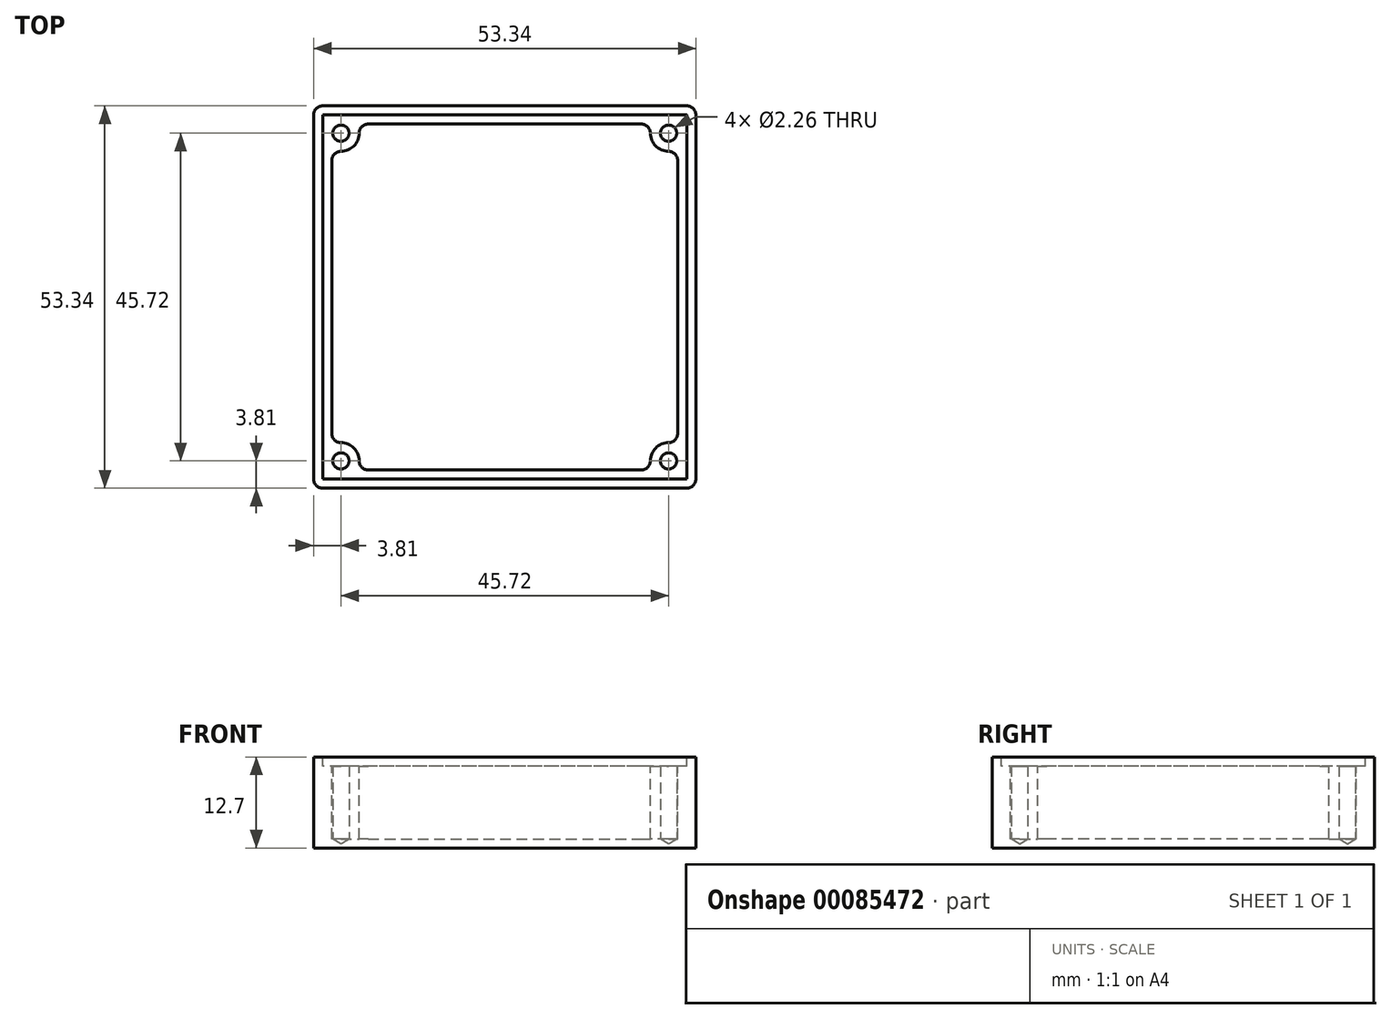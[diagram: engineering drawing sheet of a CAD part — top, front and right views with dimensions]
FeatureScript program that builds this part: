
annotation { "Feature Type Name" : "Feature", "Feature Type Description" : "" }
export const myFeature = defineFeature(function(context is Context, id is Id, definition is map)
    precondition{}
    {
        {
            var Q0;
            Q0=qCreatedBy(makeId("Top.planeOp"),FACE);
            var sketch = newSketch(context, id + "F0", { "sketchPlane" : qUnion([Q0])});
            skLineSegment(sketch, "E0.bottom", {"start": v(25.4, 25.4) * mm, "end": v(-25.4, 25.4) * mm, "construction": true});
            skLineSegment(sketch, "E0.top", {"start": v(25.4, -25.4) * mm, "end": v(-25.4, -25.4) * mm, "construction": true});
            skLineSegment(sketch, "E0.left", {"start": v(25.4, 25.4) * mm, "end": v(25.4, -25.4) * mm, "construction": true});
            skLineSegment(sketch, "E0.right", {"start": v(-25.4, 25.4) * mm, "end": v(-25.4, -25.4) * mm, "construction": true});
            skPoint(sketch, "E0.middle", {"position": v(0, 0) * mm});
            skLineSegment(sketch, "E1.bottom", {"start": v(26.67, 26.67) * mm, "end": v(-26.67, 26.67) * mm});
            skLineSegment(sketch, "E1.top", {"start": v(26.67, -26.67) * mm, "end": v(-26.67, -26.67) * mm});
            skLineSegment(sketch, "E1.left", {"start": v(26.67, 26.67) * mm, "end": v(26.67, -26.67) * mm});
            skLineSegment(sketch, "E1.right", {"start": v(-26.67, 26.67) * mm, "end": v(-26.67, -26.67) * mm});
            skSolve(sketch);
        }
        {
            var Q0;
            Q0 = qSketchRegion(id + "F0", true);
            extrude(context, id + "F1", {"entities" : qUnion([Q0]), "depth" : 12.7 * mm});
        }
        {
            var Q0;
            Q0=makeQuery(id+"F1.opExtrude","CAP_FACE",FACE,{"disambiguationData":[OSD([sQuery(id+"F0.wireOp",EDGE,"E1.bottom"),sQuery(id+"F0.wireOp",EDGE,"E1.top"),sQuery(id+"F0.wireOp",EDGE,"E1.left"),sQuery(id+"F0.wireOp",EDGE,"E1.right")])],"isStart":false});
            var sketch = newSketch(context, id + "F2", { "sketchPlane" : qUnion([Q0])});
            skPoint(sketch, "E2", {"position": v(-22.86, 22.86) * mm});
            skLineSegment(sketch, "E3", {"start": v(-22.86, 20.32) * mm, "end": v(-22.86, 20.32) * mm});
            skLineSegment(sketch, "E4", {"start": v(-20.32, 22.86) * mm, "end": v(-20.32, 22.86) * mm});
            skLineSegment(sketch, "E5", {"start": v(-19.05, 24.13) * mm, "end": v(0, 24.13) * mm});
            skLineSegment(sketch, "E6", {"start": v(-24.13, 19.05) * mm, "end": v(-24.13, 0) * mm});
            skPoint(sketch, "E7.visualSharp", {"position": v(-20.32, 24.13) * mm});
            skArc(sketch, "E7.filletArc", {"start": v(-19.05, 24.13) * mm, "mid": v(-19.95, 23.76) * mm, "end": v(-20.32, 22.86) * mm});
            skPoint(sketch, "E8.visualSharp", {"position": v(-20.32, 20.32) * mm});
            skArc(sketch, "E8.filletArc", {"start": v(-22.86, 20.32) * mm, "mid": v(-21.06, 21.06) * mm, "end": v(-20.32, 22.86) * mm});
            skPoint(sketch, "E9.visualSharp", {"position": v(-24.13, 20.32) * mm});
            skArc(sketch, "E9.filletArc", {"start": v(-22.86, 20.32) * mm, "mid": v(-23.76, 19.95) * mm, "end": v(-24.13, 19.05) * mm});
            skLineSegment(sketch, "E10.MirrorCS", {"start": v(-24.13, -19.05) * mm, "end": v(-24.13, 0) * mm});
            skArc(sketch, "E11.MirrorCS", {"start": v(-22.86, -20.32) * mm, "mid": v(-23.76, -19.95) * mm, "end": v(-24.13, -19.05) * mm});
            skLineSegment(sketch, "E12.MirrorCS", {"start": v(-22.86, -20.32) * mm, "end": v(-22.86, -20.32) * mm});
            skArc(sketch, "E13.MirrorCS", {"start": v(-22.86, -20.32) * mm, "mid": v(-21.06, -21.06) * mm, "end": v(-20.32, -22.86) * mm});
            skLineSegment(sketch, "E14.MirrorCS", {"start": v(-20.32, -22.86) * mm, "end": v(-20.32, -22.86) * mm});
            skArc(sketch, "E15.MirrorCS", {"start": v(-19.05, -24.13) * mm, "mid": v(-19.95, -23.76) * mm, "end": v(-20.32, -22.86) * mm});
            skLineSegment(sketch, "E16.MirrorCS", {"start": v(-19.05, -24.13) * mm, "end": v(0, -24.13) * mm});
            skLineSegment(sketch, "E17.MirrorCS", {"start": v(19.05, -24.13) * mm, "end": v(0, -24.13) * mm});
            skArc(sketch, "E18.MirrorCS", {"start": v(19.05, -24.13) * mm, "mid": v(19.95, -23.76) * mm, "end": v(20.32, -22.86) * mm});
            skLineSegment(sketch, "E19.MirrorCS", {"start": v(20.32, -22.86) * mm, "end": v(20.32, -22.86) * mm});
            skArc(sketch, "E20.MirrorCS", {"start": v(22.86, -20.32) * mm, "mid": v(21.06, -21.06) * mm, "end": v(20.32, -22.86) * mm});
            skLineSegment(sketch, "E21.MirrorCS", {"start": v(22.86, -20.32) * mm, "end": v(22.86, -20.32) * mm});
            skArc(sketch, "E22.MirrorCS", {"start": v(22.86, -20.32) * mm, "mid": v(23.76, -19.95) * mm, "end": v(24.13, -19.05) * mm});
            skLineSegment(sketch, "E23.MirrorCS", {"start": v(24.13, -19.05) * mm, "end": v(24.13, 0) * mm});
            skLineSegment(sketch, "E24.MirrorCS", {"start": v(24.13, 19.05) * mm, "end": v(24.13, 0) * mm});
            skLineSegment(sketch, "E25.MirrorCS", {"start": v(19.05, 24.13) * mm, "end": v(0, 24.13) * mm});
            skArc(sketch, "E26.MirrorCS", {"start": v(19.05, 24.13) * mm, "mid": v(19.95, 23.76) * mm, "end": v(20.32, 22.86) * mm});
            skLineSegment(sketch, "E27.MirrorCS", {"start": v(20.32, 22.86) * mm, "end": v(20.32, 22.86) * mm});
            skArc(sketch, "E28.MirrorCS", {"start": v(22.86, 20.32) * mm, "mid": v(21.06, 21.06) * mm, "end": v(20.32, 22.86) * mm});
            skLineSegment(sketch, "E29.MirrorCS", {"start": v(22.86, 20.32) * mm, "end": v(22.86, 20.32) * mm});
            skArc(sketch, "E30.MirrorCS", {"start": v(22.86, 20.32) * mm, "mid": v(23.76, 19.95) * mm, "end": v(24.13, 19.05) * mm});
            skSolve(sketch);
        }
        {
            var Q0;
            Q0=sQuery(id+"F2.wireOp",VERTEX,"E2");
            var Q1;
            Q1=sQuery(id+"F2.wireOp",VERTEX,"E28.MirrorCS.center");
            var Q2;
            Q2=sQuery(id+"F2.wireOp",VERTEX,"E20.MirrorCS.center");
            var Q3;
            Q3=sQuery(id+"F2.wireOp",VERTEX,"E13.MirrorCS.center");
            var Q4;
            Q4=makeQuery(id+"F1.opExtrude","SWEPT_BODY",BODY,{"disambiguationData":[OSD([sQuery(id+"F0.wireOp",EDGE,"E1.bottom"),sQuery(id+"F0.wireOp",EDGE,"E1.top"),sQuery(id+"F0.wireOp",EDGE,"E1.left"),sQuery(id+"F0.wireOp",EDGE,"E1.right")])]});
            hole(context, id + "F3", {"style" : HoleStyle.SIMPLE, "endStyle" : HoleEndStyle.BLIND, "standardTappedOrClearance" : lookupTablePath({ "standard" : "ANSI", "engagement" : "75%", "pitch" : "40 tpi", "size" : "#4", "type" : "Tapped" }), "standardBlindInLast" : lookupTablePath({ "standard" : "ANSI", "engagement" : "75%", "pitch" : "40 tpi", "size" : "#4", "type" : "Tapped" }), "holeDiameter" : 2.26 * mm, "holeDepth" : 11.43 * mm, "locations" : qUnion([Q0, Q1, Q2, Q3]), "scope" : qUnion([Q4]), "majorDiameter" : 2.84 * mm, "startStyle" : HoleStartStyle.PART});
        }
        {
            var Q0;
            Q0=makeQuery(id+"F1.opExtrude","CAP_FACE",FACE,{"disambiguationData":[OSD([sQuery(id+"F0.wireOp",EDGE,"E1.bottom"),sQuery(id+"F0.wireOp",EDGE,"E1.top"),sQuery(id+"F0.wireOp",EDGE,"E1.left"),sQuery(id+"F0.wireOp",EDGE,"E1.right")])],"isStart":false});
            var sketch = newSketch(context, id + "F4", { "sketchPlane" : qUnion([Q0])});
            skLineSegment(sketch, "E31", {"start": v(-25.4, 25.4) * mm, "end": v(-25.4, -25.4) * mm});
            skLineSegment(sketch, "E32", {"start": v(-25.4, -25.4) * mm, "end": v(25.4, -25.4) * mm});
            skLineSegment(sketch, "E33", {"start": v(25.4, -25.4) * mm, "end": v(25.4, 25.4) * mm});
            skLineSegment(sketch, "E34", {"start": v(25.4, 25.4) * mm, "end": v(-25.4, 25.4) * mm});
            skSolve(sketch);
        }
        {
            var Q0;
            Q0 = qSketchRegion(id + "F2", true);
            extrude(context, id + "F5", {"entities" : qUnion([Q0]), "operationType" : NewBodyOperationType.REMOVE, "oppositeDirection" : true, "depth" : 11.43 * mm});
        }
        {
            var Q0;
            Q0 = qSketchRegion(id + "F4", true);
            extrude(context, id + "F6", {"entities" : qUnion([Q0]), "operationType" : NewBodyOperationType.REMOVE, "oppositeDirection" : true, "depth" : 1.27 * mm});
        }
        {
            var Q0;
            Q0=makeQuery(id+"F1.opExtrude","SWEPT_EDGE",EDGE,{"disambiguationData":[OSD([sQuery(id+"F0.wireOp",EDGE,"E1.top"),sQuery(id+"F0.wireOp",EDGE,"E1.right")])]});
            var Q1;
            Q1=makeQuery(id+"F1.opExtrude","SWEPT_EDGE",EDGE,{"disambiguationData":[OSD([sQuery(id+"F0.wireOp",EDGE,"E1.top"),sQuery(id+"F0.wireOp",EDGE,"E1.left")])]});
            var Q2;
            Q2=makeQuery(id+"F1.opExtrude","SWEPT_EDGE",EDGE,{"disambiguationData":[OSD([sQuery(id+"F0.wireOp",EDGE,"E1.bottom"),sQuery(id+"F0.wireOp",EDGE,"E1.left")])]});
            var Q3;
            Q3=makeQuery(id+"F1.opExtrude","SWEPT_EDGE",EDGE,{"disambiguationData":[OSD([sQuery(id+"F0.wireOp",EDGE,"E1.bottom"),sQuery(id+"F0.wireOp",EDGE,"E1.right")])]});
            fillet(context, id + "F7", {"entities" : qUnion([Q0, Q1, Q2, Q3]), "radius" : 1.27 * mm, "tangentPropagation" : true, "allowEdgeOverflow" : false});
        }
    });
